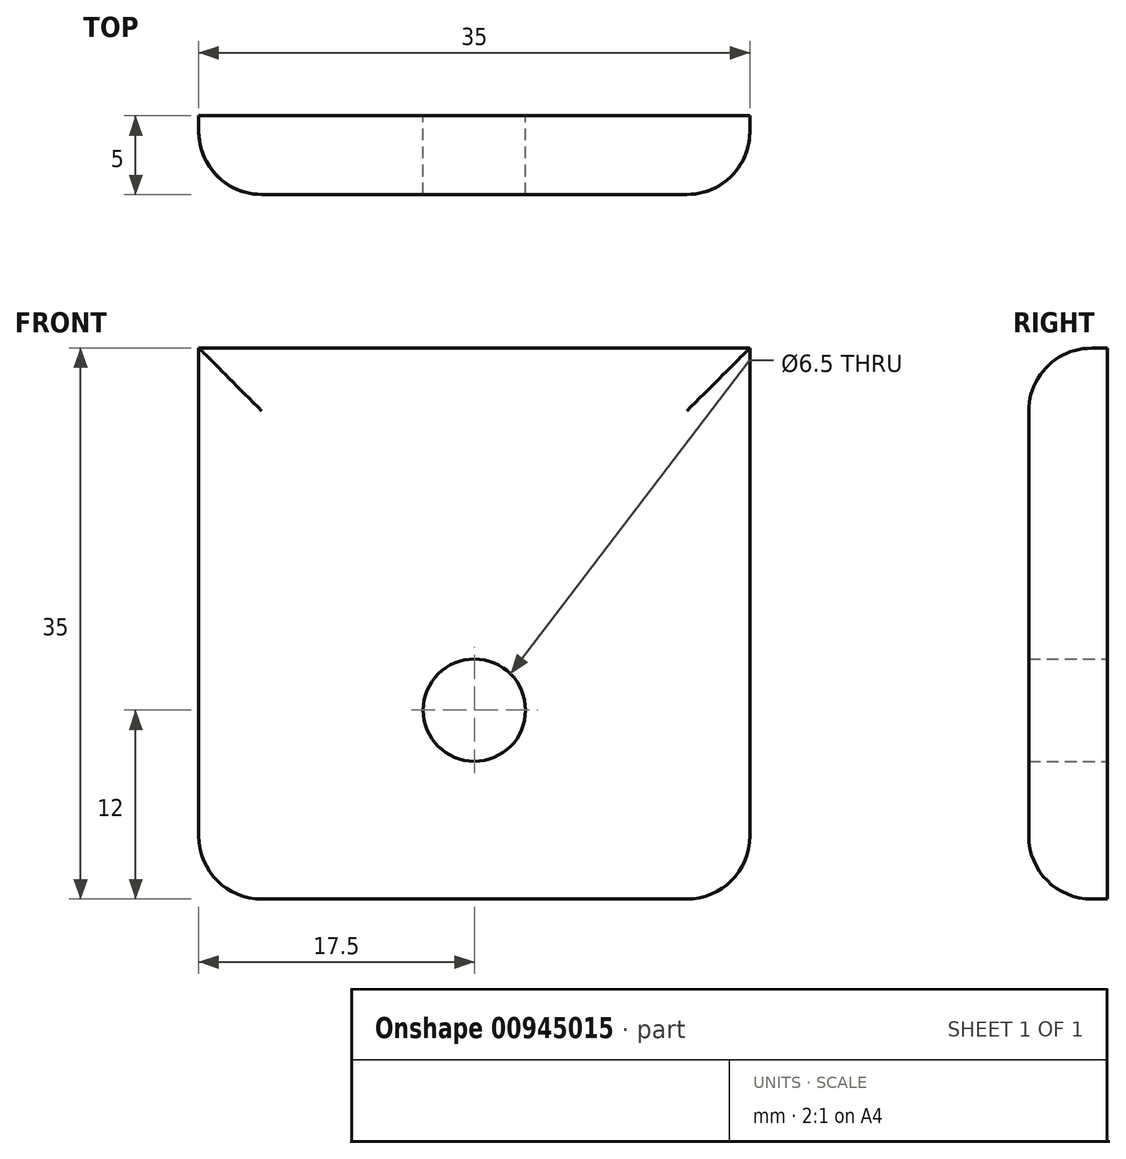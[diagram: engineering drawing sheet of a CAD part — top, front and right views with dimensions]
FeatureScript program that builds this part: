
annotation { "Feature Type Name" : "Feature", "Feature Type Description" : "" }
export const myFeature = defineFeature(function(context is Context, id is Id, definition is map)
    precondition{}
    {
        {
            var Q0;
            Q0=qCreatedBy(makeId("Front.planeOp"),FACE);
            var sketch = newSketch(context, id + "F0", { "sketchPlane" : qUnion([Q0])});
            skLineSegment(sketch, "E0.bottom", {"start": v(17.5, -17.5) * mm, "end": v(-17.5, -17.5) * mm});
            skLineSegment(sketch, "E0.top", {"start": v(17.5, 17.5) * mm, "end": v(-17.5, 17.5) * mm});
            skLineSegment(sketch, "E0.left", {"start": v(17.5, -17.5) * mm, "end": v(17.5, 17.5) * mm});
            skLineSegment(sketch, "E0.right", {"start": v(-17.5, -17.5) * mm, "end": v(-17.5, 17.5) * mm});
            skPoint(sketch, "E0.middle", {"position": v(0, 0) * mm});
            skLineSegment(sketch, "E1", {"start": v(0, -17.5) * mm, "end": v(0, -5.5) * mm});
            skCircle(sketch, "E2", {"center": v(0, -5.5) * mm, "radius": 3.25 * mm});
            skSolve(sketch);
        }
        {
            var Q0;
            Q0=makeQuery(id+"F0.imprint","IMPRINT",FACE,{"disambiguationData":[TD([[makeQuery(id+"F0.imprint","IMPRINT",EDGE,{"derivedFrom":sQuery(id+"F0.wireOp",EDGE,"E0.top")}),1.0]])]});
            extrude(context, id + "F1", {"entities" : qUnion([Q0]), "depth" : 5 * mm, "offsetDistance" : 25 * mm});
        }
        {
            var Q0;
            Q0=makeQuery(id+"F1.opExtrude","CAP_EDGE",EDGE,{"disambiguationData":[OSD([sQuery(id+"F0.wireOp",EDGE,"E0.right")])],"isStart":false});
            var Q1;
            Q1=makeQuery(id+"F1.opExtrude","CAP_EDGE",EDGE,{"disambiguationData":[OSD([sQuery(id+"F0.wireOp",EDGE,"E0.left")])],"isStart":false});
            var Q2;
            Q2=makeQuery(id+"F1.opExtrude","CAP_EDGE",EDGE,{"disambiguationData":[OSD([sQuery(id+"F0.wireOp",EDGE,"E0.bottom")])],"isStart":false});
            var Q3;
            Q3=makeQuery(id+"F1.opExtrude","CAP_EDGE",EDGE,{"disambiguationData":[OSD([sQuery(id+"F0.wireOp",EDGE,"E0.top")])],"isStart":false});
            var Q4;
            Q4=makeQuery(id+"F1.opExtrude","SWEPT_EDGE",EDGE,{"disambiguationData":[OSD([sQuery(id+"F0.wireOp",EDGE,"E0.bottom"),sQuery(id+"F0.wireOp",EDGE,"E0.right")])]});
            var Q5;
            Q5=makeQuery(id+"F1.opExtrude","SWEPT_EDGE",EDGE,{"disambiguationData":[OSD([sQuery(id+"F0.wireOp",EDGE,"E0.bottom"),sQuery(id+"F0.wireOp",EDGE,"E0.left")])]});
            fillet(context, id + "F2", {"entities" : qUnion([Q0, Q1, Q2, Q3, Q4, Q5]), "radius" : 4 * mm, "tangentPropagation" : true, "allowEdgeOverflow" : false});
        }
    });
